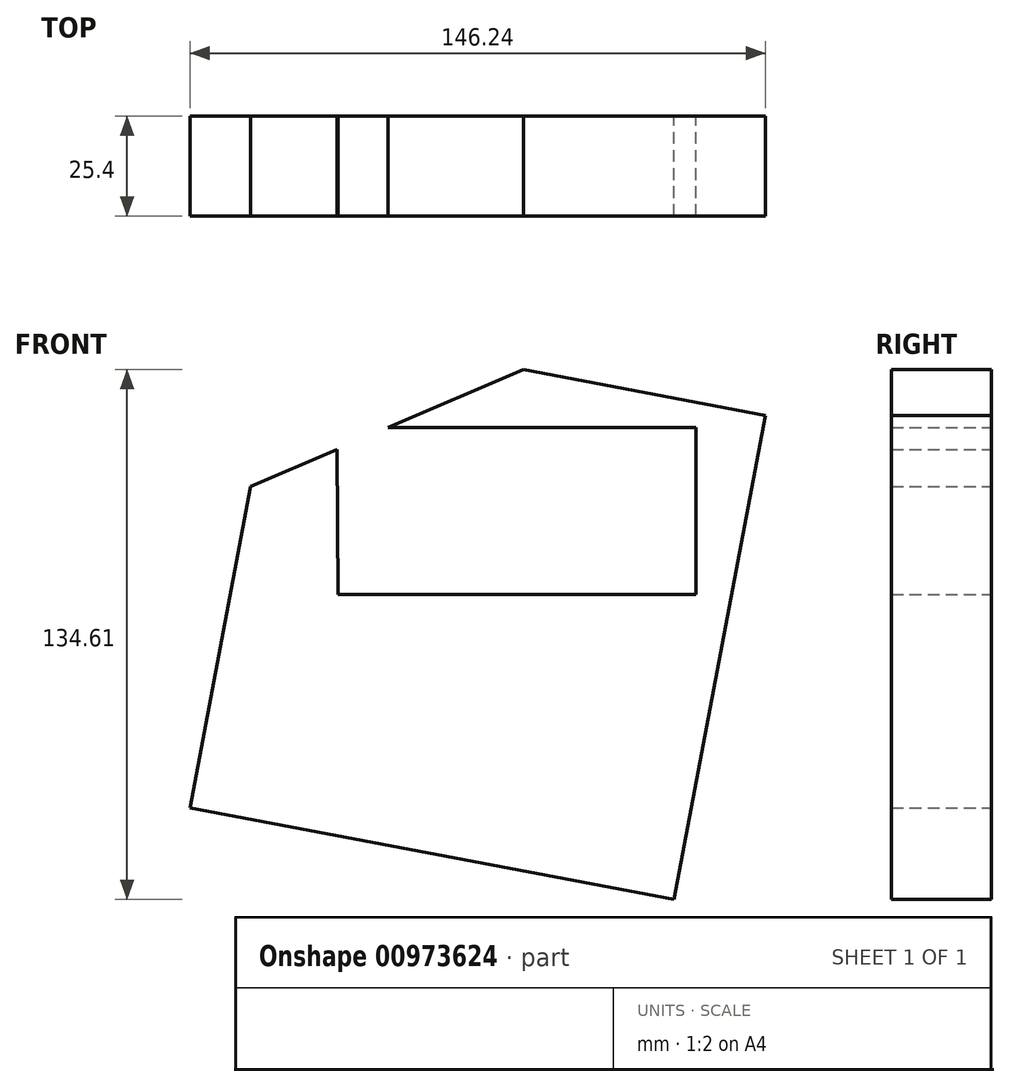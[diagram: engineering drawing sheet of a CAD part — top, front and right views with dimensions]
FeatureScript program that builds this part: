
annotation { "Feature Type Name" : "Feature", "Feature Type Description" : "" }
export const myFeature = defineFeature(function(context is Context, id is Id, definition is map)
    precondition{}
    {
        {
            var Q0;
            Q0=qCreatedBy(makeId("Front.planeOp"),FACE);
            var sketch = newSketch(context, id + "F0", { "sketchPlane" : qUnion([Q0])});
            skLineSegment(sketch, "E0", {"start": v(-37.3, 34.26) * mm, "end": v(53.96, 34.26) * mm});
            skLineSegment(sketch, "E1", {"start": v(53.96, 34.26) * mm, "end": v(53.96, -50.48) * mm});
            skLineSegment(sketch, "E2", {"start": v(53.96, -50.48) * mm, "end": v(-36.57, -50.48) * mm});
            skLineSegment(sketch, "E3", {"start": v(-36.57, -50.48) * mm, "end": v(-37.3, 34.26) * mm});
            skLineSegment(sketch, "E4", {"start": v(-36.94, -8.11) * mm, "end": v(53.96, -8.11) * mm});
            skSolve(sketch);
        }
        {
            var Q0;
            {var subQ0=sQuery(id+"F0.wireOp",EDGE,"E0");Q0=makeQuery(id+"F0.imprint","IMPRINT",FACE,{"disambiguationData":[TD([[makeQuery(id+"F0.imprint","IMPRINT",EDGE,{"derivedFrom":subQ0}),-1.0]])]});}
            var sketch = newSketch(context, id + "F1", { "sketchPlane" : qUnion([Q0])});
            skLineSegment(sketch, "E5", {"start": v(-51.37, 60.6) * mm, "end": v(71.63, 37.36) * mm});
            skLineSegment(sketch, "E6", {"start": v(71.63, 37.36) * mm, "end": v(48.38, -85.63) * mm});
            skLineSegment(sketch, "E7", {"start": v(48.38, -85.63) * mm, "end": v(-74.61, -62.39) * mm});
            skLineSegment(sketch, "E8", {"start": v(-74.61, -62.39) * mm, "end": v(-51.37, 60.6) * mm});
            skLineSegment(sketch, "E9", {"start": v(10.13, 48.98) * mm, "end": v(-59.17, 19.32) * mm});
            skSolve(sketch);
        }
        {
            var Q0;
            {var subQ10=sQuery(id+"F1.wireOp",EDGE,"E6");Q0=makeQuery(id+"F1.imprint","IMPRINT",FACE,{"disambiguationData":[TD([[makeQuery(id+"F1.imprint","IMPRINT",EDGE,{"derivedFrom":subQ10}),-1.0]])]});}
            extrude(context, id + "F2", {"entities" : qUnion([Q0]), "depth" : 25.4 * mm, "offsetDistance" : 25.4 * mm});
        }
    });
